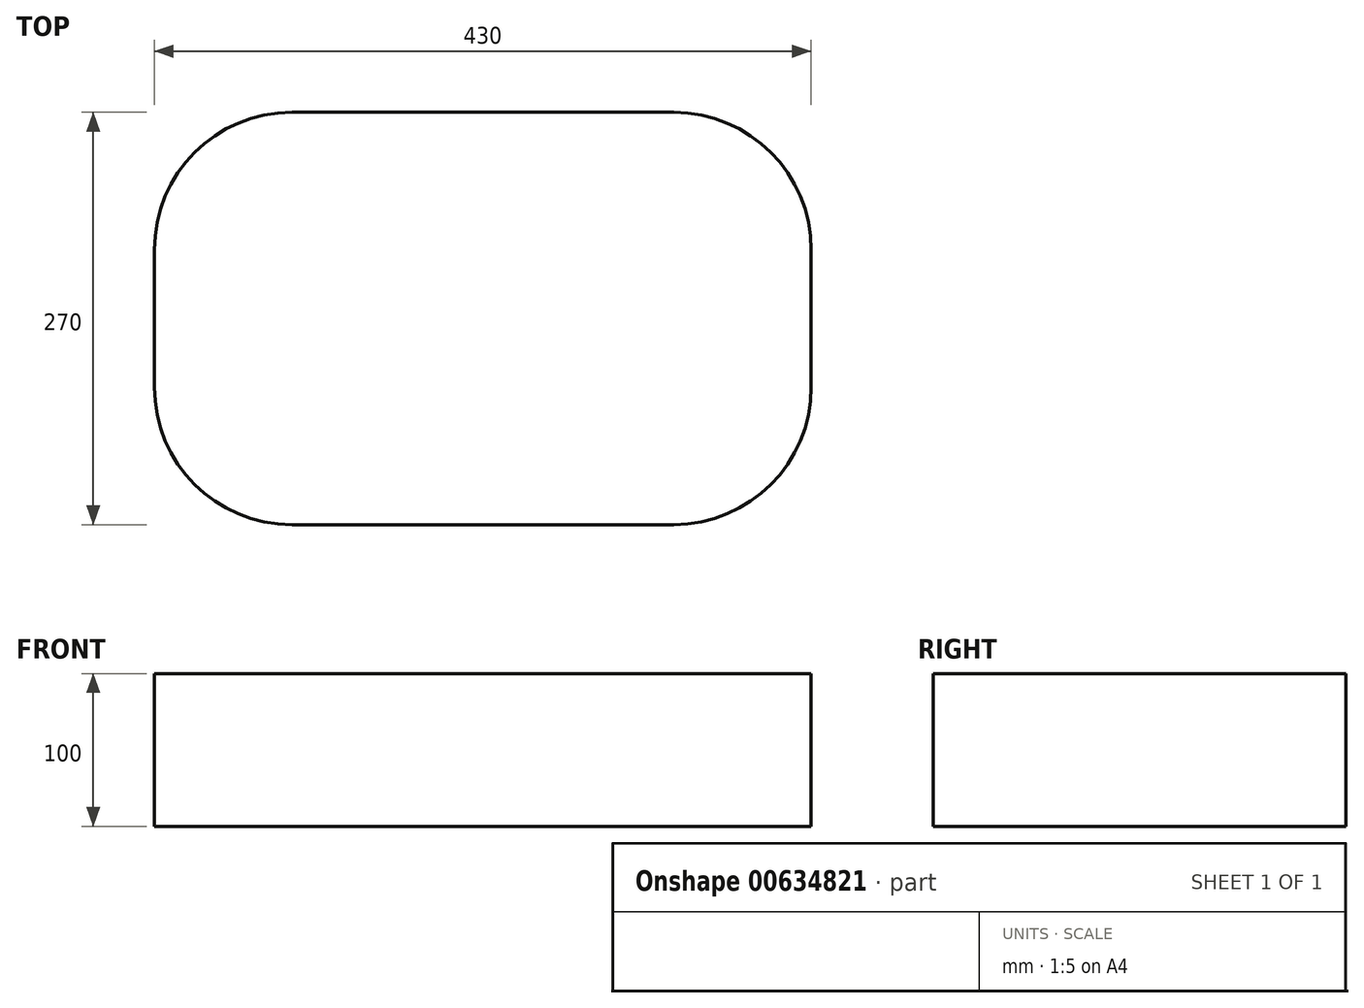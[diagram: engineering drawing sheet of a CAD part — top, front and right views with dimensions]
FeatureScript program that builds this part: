
annotation { "Feature Type Name" : "Feature", "Feature Type Description" : "" }
export const myFeature = defineFeature(function(context is Context, id is Id, definition is map)
    precondition{}
    {
        {
            var Q0;
            Q0=qCreatedBy(makeId("Top.planeOp"),FACE);
            var sketch = newSketch(context, id + "F0", { "sketchPlane" : qUnion([Q0])});
            skLineSegment(sketch, "E0.bottom", {"start": v(125, -135) * mm, "end": v(-125, -135) * mm});
            skLineSegment(sketch, "E0.top", {"start": v(125, 135) * mm, "end": v(-125, 135) * mm});
            skLineSegment(sketch, "E0.left", {"start": v(215, -45) * mm, "end": v(215, 45) * mm});
            skLineSegment(sketch, "E0.right", {"start": v(-215, -45) * mm, "end": v(-215, 45) * mm});
            skPoint(sketch, "E0.middle", {"position": v(0, 0) * mm});
            skPoint(sketch, "E1.visualSharp", {"position": v(-215, -135) * mm});
            skArc(sketch, "E1.filletArc", {"start": v(-215, -45) * mm, "mid": v(-188.64, -108.64) * mm, "end": v(-125, -135) * mm});
            skPoint(sketch, "E2.visualSharp", {"position": v(215, -135) * mm});
            skArc(sketch, "E2.filletArc", {"start": v(125, -135) * mm, "mid": v(188.64, -108.64) * mm, "end": v(215, -45) * mm});
            skPoint(sketch, "E3.visualSharp", {"position": v(215, 135) * mm});
            skArc(sketch, "E3.filletArc", {"start": v(215, 45) * mm, "mid": v(188.64, 108.64) * mm, "end": v(125, 135) * mm});
            skPoint(sketch, "E4.visualSharp", {"position": v(-215, 135) * mm});
            skArc(sketch, "E4.filletArc", {"start": v(-125, 135) * mm, "mid": v(-188.64, 108.64) * mm, "end": v(-215, 45) * mm});
            skSolve(sketch);
        }
        {
            var Q0;
            Q0=makeQuery(id+"F0.imprint","IMPRINT",FACE,{"disambiguationData":[TD([[makeQuery(id+"F0.imprint","IMPRINT",EDGE,{"derivedFrom":sQuery(id+"F0.wireOp",EDGE,"E0.bottom")}),-1.0]])]});
            extrude(context, id + "F1", {"entities" : qUnion([Q0]), "depth" : 100 * mm, "offsetDistance" : 25 * mm});
        }
    });
